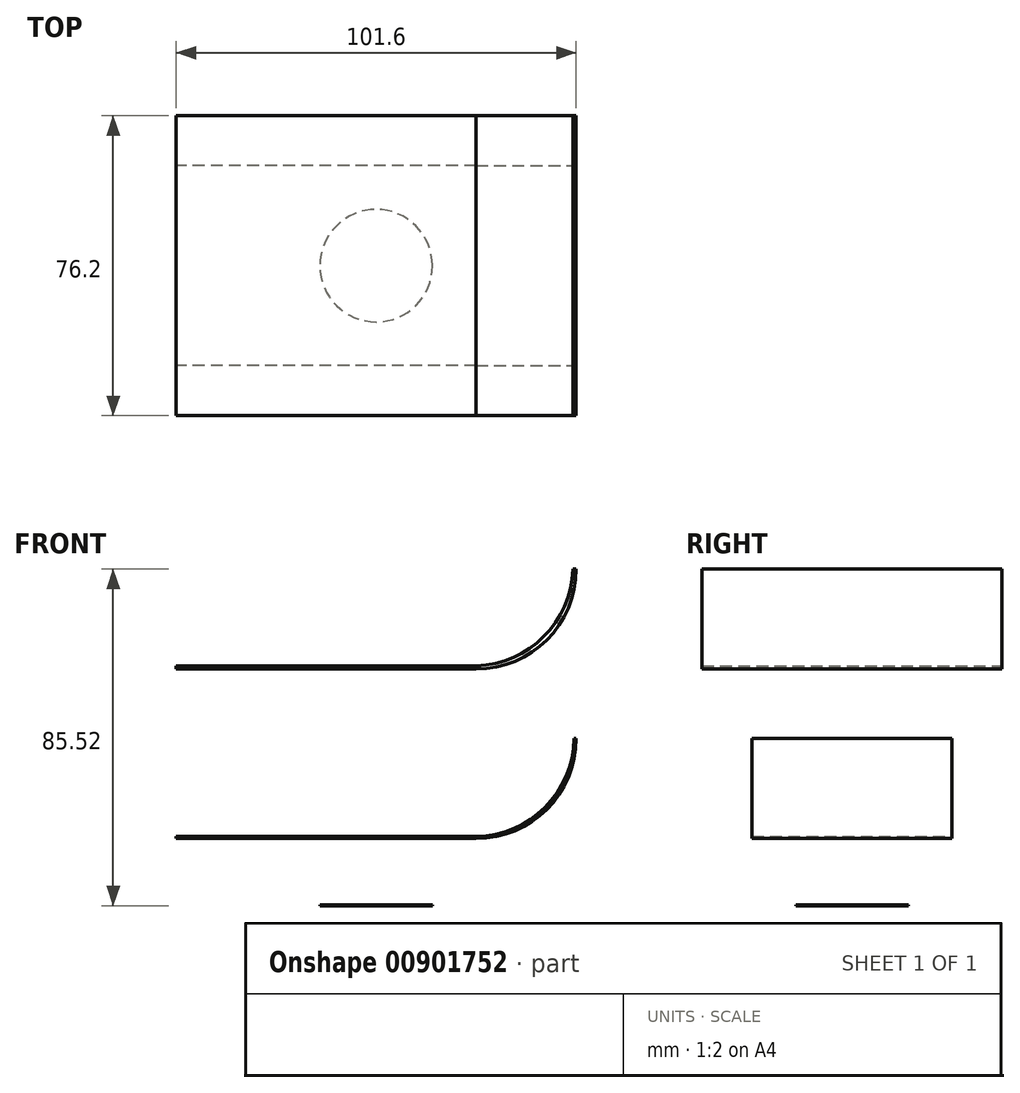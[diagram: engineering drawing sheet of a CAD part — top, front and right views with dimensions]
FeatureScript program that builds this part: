
annotation { "Feature Type Name" : "Feature", "Feature Type Description" : "" }
export const myFeature = defineFeature(function(context is Context, id is Id, definition is map)
    precondition{}
    {
        {
            var Q0;
            Q0=qCreatedBy(makeId("Top.planeOp"),FACE);
            var sketch = newSketch(context, id + "F0", { "sketchPlane" : qUnion([Q0])});
            skCircle(sketch, "E0", {"center": v(0, 0) * mm, "radius": 14.29 * mm});
            skSolve(sketch);
        }
        {
            var Q0;
            Q0=qSketchRegion(id+"F0",true);
            extrude(context, id + "F1", {"entities" : qUnion([Q0]), "depth" : 0.25 * mm});
        }
        {
            var Q0;
            Q0=qCreatedBy(makeId("Front.planeOp"),FACE);
            var sketch = newSketch(context, id + "F2", { "sketchPlane" : qUnion([Q0])});
            skLineSegment(sketch, "E1.bottom", {"start": v(50.8, 42.47) * mm, "end": v(50.3, 42.47) * mm});
            skLineSegment(sketch, "E1.top", {"start": v(25.4, 17.07) * mm, "end": v(-50.8, 17.07) * mm});
            skLineSegment(sketch, "E1.left", {"start": v(50.8, 42.47) * mm, "end": v(50.8, 42.47) * mm});
            skLineSegment(sketch, "E1.right", {"start": v(-50.8, 17.57) * mm, "end": v(-50.8, 17.07) * mm});
            skPoint(sketch, "E1.middle", {"position": v(0, 29.77) * mm});
            skPoint(sketch, "E2", {"position": v(28.14, 29.77) * mm});
            skPoint(sketch, "E3", {"position": v(28.14, 17.07) * mm});
            skPoint(sketch, "E4", {"position": v(28.14, 42.47) * mm});
            skPoint(sketch, "E5.visualSharp", {"position": v(50.8, 17.07) * mm});
            skArc(sketch, "E5.filletArc", {"start": v(25.4, 17.07) * mm, "mid": v(43.36, 24.5) * mm, "end": v(50.8, 42.47) * mm});
            skArc(sketch, "E6", {"start": v(25.4, 17.57) * mm, "mid": v(42.86, 25) * mm, "end": v(50.3, 42.47) * mm});
            skLineSegment(sketch, "E7", {"start": v(25.4, 17.57) * mm, "end": v(-50.8, 17.57) * mm});
            skPoint(sketch, "E8.orphan", {"position": v(-50.8, 42.47) * mm});
            skSolve(sketch);
        }
        {
            var Q0;
            Q0=qSketchRegion(id+"F2",true);
            extrude(context, id + "F3", {"entities" : qUnion([Q0]), "endBound" : BoundingType.SYMMETRIC, "depth" : 50.8 * mm});
        }
        {
            var Q0;
            Q0=qCreatedBy(makeId("Front.planeOp"),FACE);
            var sketch = newSketch(context, id + "F4", { "sketchPlane" : qUnion([Q0])});
            skLineSegment(sketch, "E9.bottom", {"start": v(25.4, 60.12) * mm, "end": v(-50.8, 60.12) * mm});
            skLineSegment(sketch, "E9.top", {"start": v(50.8, 85.52) * mm, "end": v(49.99, 85.52) * mm});
            skLineSegment(sketch, "E9.left", {"start": v(50.8, 85.52) * mm, "end": v(50.8, 85.52) * mm});
            skLineSegment(sketch, "E9.right", {"start": v(-50.8, 60.12) * mm, "end": v(-50.8, 60.93) * mm});
            skPoint(sketch, "E9.middle", {"position": v(0, 72.82) * mm});
            skPoint(sketch, "E10.visualSharp", {"position": v(50.8, 60.12) * mm});
            skArc(sketch, "E10.filletArc", {"start": v(25.4, 60.12) * mm, "mid": v(43.36, 67.56) * mm, "end": v(50.8, 85.52) * mm});
            skArc(sketch, "E11", {"start": v(25.4, 60.93) * mm, "mid": v(42.56, 68.36) * mm, "end": v(49.99, 85.52) * mm});
            skLineSegment(sketch, "E12", {"start": v(25.4, 60.93) * mm, "end": v(-50.8, 60.93) * mm});
            skPoint(sketch, "E13.trimOffspring.end.orphan", {"position": v(-50.8, 85.52) * mm});
            skSolve(sketch);
        }
        {
            var Q0;
            Q0=qSketchRegion(id+"F4",true);
            extrude(context, id + "F5", {"entities" : qUnion([Q0]), "endBound" : BoundingType.SYMMETRIC, "depth" : 76.2 * mm});
        }
    });
